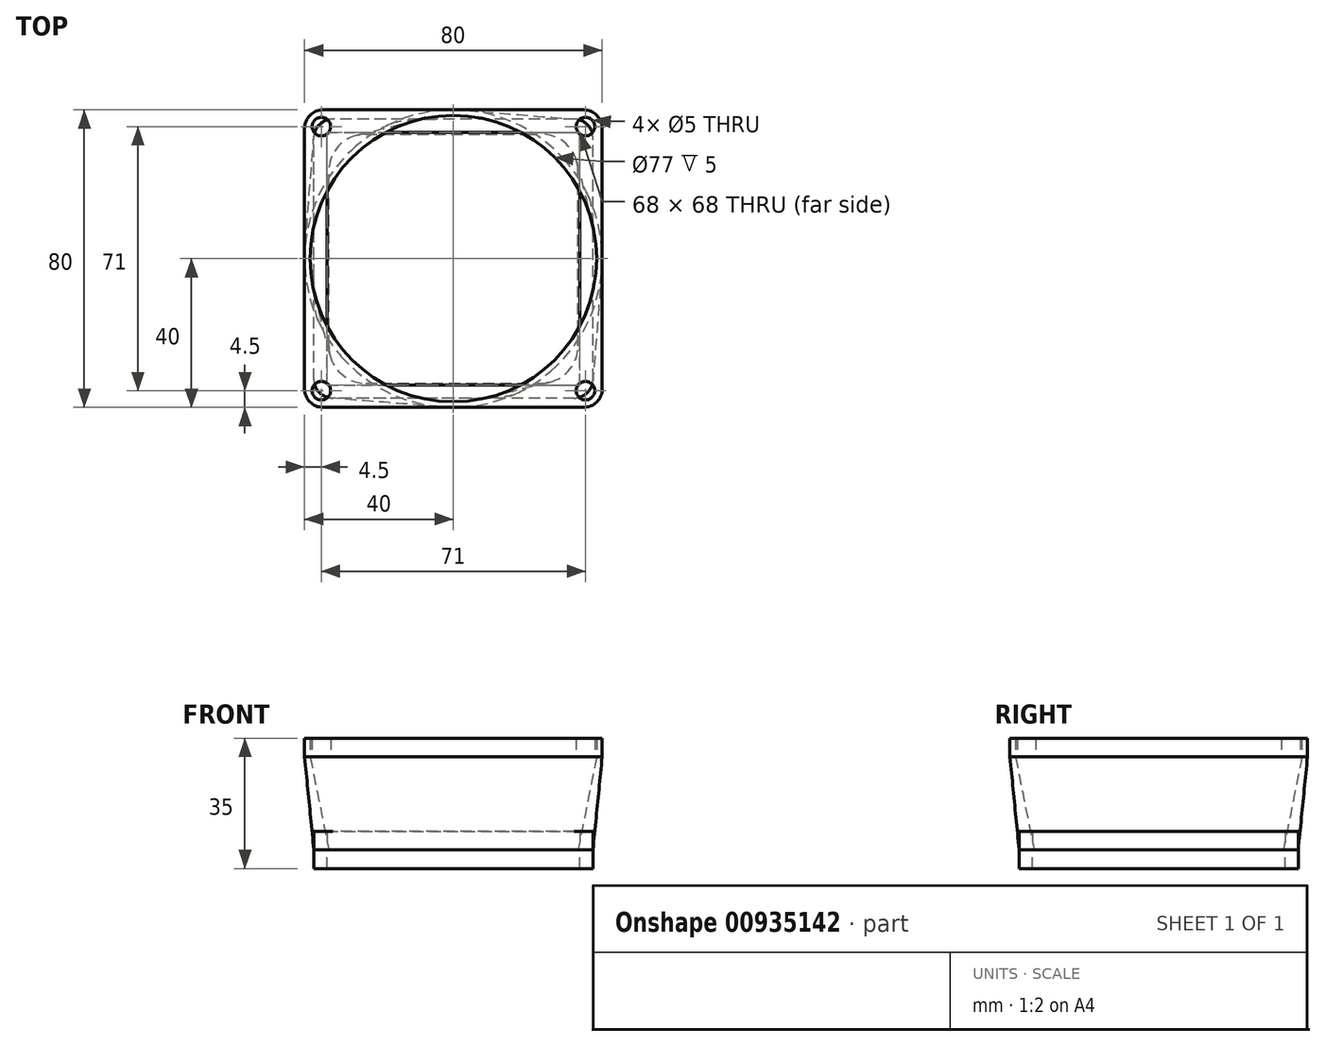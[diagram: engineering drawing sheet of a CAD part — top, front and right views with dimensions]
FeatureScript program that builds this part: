
annotation { "Feature Type Name" : "Feature", "Feature Type Description" : "" }
export const myFeature = defineFeature(function(context is Context, id is Id, definition is map)
    precondition{}
    {
        {
            var Q0;
            Q0=qCreatedBy(makeId("Top.planeOp"),FACE);
            cPlane(context, id + "F0", {"entities" : qUnion([Q0]), "cplaneType" : CPlaneType.OFFSET, "offset" : 25 * mm, "oppositeDirection" : true, "width" : 150 * mm, "height" : 150 * mm});
        }
        {
            var Q0;
            Q0=qCreatedBy(makeId("Top.planeOp"),FACE);
            var sketch = newSketch(context, id + "F1", { "sketchPlane" : qUnion([Q0])});
            skLineSegment(sketch, "E0.bottom", {"start": v(35, -40) * mm, "end": v(-35, -40) * mm});
            skLineSegment(sketch, "E0.top", {"start": v(35, 40) * mm, "end": v(-35, 40) * mm});
            skLineSegment(sketch, "E0.left", {"start": v(40, -35) * mm, "end": v(40, 35) * mm});
            skLineSegment(sketch, "E0.right", {"start": v(-40, -35) * mm, "end": v(-40, 35) * mm});
            skPoint(sketch, "E0.middle", {"position": v(0, 0) * mm});
            skPoint(sketch, "E1.visualSharp", {"position": v(40, -40) * mm});
            skArc(sketch, "E1.filletArc", {"start": v(35, -40) * mm, "mid": v(38.54, -38.54) * mm, "end": v(40, -35) * mm});
            skPoint(sketch, "E2.visualSharp", {"position": v(40, 40) * mm});
            skArc(sketch, "E2.filletArc", {"start": v(40, 35) * mm, "mid": v(38.54, 38.54) * mm, "end": v(35, 40) * mm});
            skPoint(sketch, "E3.visualSharp", {"position": v(-40, 40) * mm});
            skArc(sketch, "E3.filletArc", {"start": v(-35, 40) * mm, "mid": v(-38.54, 38.54) * mm, "end": v(-40, 35) * mm});
            skPoint(sketch, "E4.visualSharp", {"position": v(-40, -40) * mm});
            skArc(sketch, "E4.filletArc", {"start": v(-40, -35) * mm, "mid": v(-38.54, -38.54) * mm, "end": v(-35, -40) * mm});
            skSolve(sketch);
        }
        {
            var Q0;
            Q0=qCreatedBy(id+"F0.planeOp",FACE);
            var sketch = newSketch(context, id + "F2", { "sketchPlane" : qUnion([Q0])});
            skLineSegment(sketch, "E5.bottom", {"start": v(-23.5, -33.5) * mm, "end": v(23.5, -33.5) * mm});
            skLineSegment(sketch, "E5.top", {"start": v(-23.5, 33.5) * mm, "end": v(23.5, 33.5) * mm});
            skLineSegment(sketch, "E5.left", {"start": v(-33.5, -23.5) * mm, "end": v(-33.5, 23.5) * mm});
            skLineSegment(sketch, "E5.right", {"start": v(33.5, -23.5) * mm, "end": v(33.5, 23.5) * mm});
            skPoint(sketch, "E5.middle", {"position": v(0, 0) * mm});
            skPoint(sketch, "E6.visualSharp", {"position": v(-33.5, 33.5) * mm});
            skArc(sketch, "E6.filletArc", {"start": v(-23.5, 33.5) * mm, "mid": v(-30.57, 30.57) * mm, "end": v(-33.5, 23.5) * mm});
            skPoint(sketch, "E7.visualSharp", {"position": v(33.5, 33.5) * mm});
            skArc(sketch, "E7.filletArc", {"start": v(33.5, 23.5) * mm, "mid": v(30.57, 30.57) * mm, "end": v(23.5, 33.5) * mm});
            skPoint(sketch, "E8.visualSharp", {"position": v(33.5, -33.5) * mm});
            skArc(sketch, "E8.filletArc", {"start": v(23.5, -33.5) * mm, "mid": v(30.57, -30.57) * mm, "end": v(33.5, -23.5) * mm});
            skPoint(sketch, "E9.visualSharp", {"position": v(-33.5, -33.5) * mm});
            skArc(sketch, "E9.filletArc", {"start": v(-33.5, -23.5) * mm, "mid": v(-30.57, -30.57) * mm, "end": v(-23.5, -33.5) * mm});
            skSolve(sketch);
        }
        {
            var Q0;
            Q0=qCreatedBy(makeId("Top.planeOp"),FACE);
            var sketch = newSketch(context, id + "F3", { "sketchPlane" : qUnion([Q0])});
            skCircle(sketch, "E10", {"center": v(0, 0) * mm, "radius": 38.5 * mm});
            skSolve(sketch);
        }
        {
            var Q0;
            Q0=qCreatedBy(id+"F0.planeOp",FACE);
            var sketch = newSketch(context, id + "F4", { "sketchPlane" : qUnion([Q0])});
            skLineSegment(sketch, "E11.bottom", {"start": v(32.5, -37.5) * mm, "end": v(-32.5, -37.5) * mm});
            skLineSegment(sketch, "E11.top", {"start": v(32.5, 37.5) * mm, "end": v(-32.5, 37.5) * mm});
            skLineSegment(sketch, "E11.left", {"start": v(37.5, -32.5) * mm, "end": v(37.5, 32.5) * mm});
            skLineSegment(sketch, "E11.right", {"start": v(-37.5, -32.5) * mm, "end": v(-37.5, 32.5) * mm});
            skPoint(sketch, "E11.middle", {"position": v(0, 0) * mm});
            skPoint(sketch, "E12.visualSharp", {"position": v(37.5, -37.5) * mm});
            skArc(sketch, "E12.filletArc", {"start": v(32.5, -37.5) * mm, "mid": v(36.04, -36.04) * mm, "end": v(37.5, -32.5) * mm});
            skPoint(sketch, "E13.visualSharp", {"position": v(37.5, 37.5) * mm});
            skArc(sketch, "E13.filletArc", {"start": v(37.5, 32.5) * mm, "mid": v(36.04, 36.04) * mm, "end": v(32.5, 37.5) * mm});
            skPoint(sketch, "E14.visualSharp", {"position": v(-37.5, 37.5) * mm});
            skArc(sketch, "E14.filletArc", {"start": v(-32.5, 37.5) * mm, "mid": v(-36.04, 36.04) * mm, "end": v(-37.5, 32.5) * mm});
            skPoint(sketch, "E15.visualSharp", {"position": v(-37.5, -37.5) * mm});
            skArc(sketch, "E15.filletArc", {"start": v(-37.5, -32.5) * mm, "mid": v(-36.04, -36.04) * mm, "end": v(-32.5, -37.5) * mm});
            skSolve(sketch);
        }
        {
            var Q0;
            Q0=qCreatedBy(makeId("Top.planeOp"),FACE);
            var sketch = newSketch(context, id + "F5", { "sketchPlane" : qUnion([Q0])});
            skCircle(sketch, "E16", {"center": v(0, 0) * mm, "radius": 40 * mm});
            skSolve(sketch);
        }
        {
            var Q0;
            Q0=qCreatedBy(id+"F0.planeOp",FACE);
            var sketch = newSketch(context, id + "F6", { "sketchPlane" : qUnion([Q0])});
            skLineSegment(sketch, "E17.bottom", {"start": v(-34, -34) * mm, "end": v(34, -34) * mm});
            skLineSegment(sketch, "E17.top", {"start": v(-34, 34) * mm, "end": v(34, 34) * mm});
            skLineSegment(sketch, "E17.left", {"start": v(-34, -34) * mm, "end": v(-34, 34) * mm});
            skLineSegment(sketch, "E17.right", {"start": v(34, -34) * mm, "end": v(34, 34) * mm});
            skPoint(sketch, "E17.middle", {"position": v(0, 0) * mm});
            skSolve(sketch);
        }
        {
            var Q0;
            Q0=qSketchRegion(id+"F8",true);
            var Q1;
            Q1=qSketchRegion(id+"F1",true);
            extrude(context, id + "F7", {"entities" : qUnion([Q0, Q1]), "depth" : 5 * mm, "offsetDistance" : 25 * mm});
        }
        {
            var Q0;
            Q0=qCreatedBy(makeId("Top.planeOp"),FACE);
            var sketch = newSketch(context, id + "F8", { "sketchPlane" : qUnion([Q0])});
            skCircle(sketch, "E18", {"center": v(-35.5, 35.5) * mm, "radius": 2.5 * mm});
            skCircle(sketch, "E19", {"center": v(35.5, 35.5) * mm, "radius": 2.5 * mm});
            skCircle(sketch, "E20", {"center": v(35.5, -35.5) * mm, "radius": 2.5 * mm});
            skCircle(sketch, "E21", {"center": v(-35.5, -35.5) * mm, "radius": 2.5 * mm});
            skSolve(sketch);
        }
        {
            var Q0;
            Q0=qSketchRegion(id+"F3",true);
            var Q1;
            Q1=qSketchRegion(id+"F6",true);
            var Q2;
            Q2=qSketchRegion(id+"F4",true);
            extrude(context, id + "F9", {"entities" : qUnion([Q0, Q1, Q2]), "depth" : 5 * mm, "offsetDistance" : 25 * mm});
        }
        {
            var Q0;
            Q0=qSketchRegion(id+"F8",true);
            extrude(context, id + "F10", {"entities" : qUnion([Q0]), "depth" : 5 * mm, "offsetDistance" : 25 * mm});
        }
        {
            var Q0;
            Q0=makeQuery(id+"F9.opExtrude","SWEPT_BODY",BODY,{"disambiguationData":[OSD([sQuery(id+"F3.wireOp",EDGE,"E10")])]});
            var Q1;
            Q1=makeQuery(id+"F10.opExtrude","SWEPT_BODY",BODY,{"disambiguationData":[OSD([sQuery(id+"F8.wireOp",EDGE,"E19")])]});
            var Q2;
            Q2=makeQuery(id+"F10.opExtrude","SWEPT_BODY",BODY,{"disambiguationData":[OSD([sQuery(id+"F8.wireOp",EDGE,"E21")])]});
            var Q3;
            Q3=makeQuery(id+"F10.opExtrude","SWEPT_BODY",BODY,{"disambiguationData":[OSD([sQuery(id+"F8.wireOp",EDGE,"E18")])]});
            var Q4;
            Q4=makeQuery(id+"F10.opExtrude","SWEPT_BODY",BODY,{"disambiguationData":[OSD([sQuery(id+"F8.wireOp",EDGE,"E20")])]});
            var Q5;
            Q5=makeQuery(id+"F7.opExtrude","SWEPT_BODY",BODY,{"disambiguationData":[OSD([sQuery(id+"F1.wireOp",EDGE,"E0.bottom"),sQuery(id+"F1.wireOp",EDGE,"E0.top"),sQuery(id+"F1.wireOp",EDGE,"E0.left"),sQuery(id+"F1.wireOp",EDGE,"E0.right"),sQuery(id+"F1.wireOp",EDGE,"E1.filletArc"),sQuery(id+"F1.wireOp",EDGE,"E2.filletArc"),sQuery(id+"F1.wireOp",EDGE,"E3.filletArc"),sQuery(id+"F1.wireOp",EDGE,"E4.filletArc")])]});
            booleanBodies(context, id + "F11", {"operationType" : BooleanOperationType.SUBTRACTION, "tools" : qUnion([Q0, Q1, Q2, Q3, Q4]), "targets" : qUnion([Q5])});
        }
        {
            var Q0;
            Q0=qSketchRegion(id+"F3",true);
            var Q1;
            Q1=qSketchRegion(id+"F2",true);
            loft(context, id + "F12", {"sheetProfilesArray" : [{ "sheetProfileEntities" : qUnion([Q0]) }, { "sheetProfileEntities" : qUnion([Q1]) }]});
        }
        {
            var Q0;
            Q0=qSketchRegion(id+"F5",true);
            var Q1;
            Q1=qSketchRegion(id+"F4",true);
            loft(context, id + "F13", {"sheetProfilesArray" : [{ "sheetProfileEntities" : qUnion([Q0]) }, { "sheetProfileEntities" : qUnion([Q1]) }]});
        }
        {
            var Q0;
            Q0=makeQuery(id+"F12.opLoft","SWEPT_BODY",BODY,{"disambiguationData":[OSD([makeQuery(id+"F2.imprint","IMPRINT",FACE,{"disambiguationData":[TD([[makeQuery(id+"F2.imprint","IMPRINT",EDGE,{"derivedFrom":sQuery(id+"F2.wireOp",EDGE,"E5.bottom")}),1.0]])]}),makeQuery(id+"F3.imprint","IMPRINT",FACE,{"disambiguationData":[TD([[makeQuery(id+"F3.imprint","IMPRINT",EDGE,{"derivedFrom":sQuery(id+"F3.wireOp",EDGE,"E10")}),1.0]])]})])]});
            var Q1;
            Q1=makeQuery(id+"F13.opLoft","SWEPT_BODY",BODY,{"disambiguationData":[OSD([makeQuery(id+"F4.imprint","IMPRINT",FACE,{"disambiguationData":[TD([[makeQuery(id+"F4.imprint","IMPRINT",EDGE,{"derivedFrom":sQuery(id+"F4.wireOp",EDGE,"E11.bottom")}),-1.0]])]}),makeQuery(id+"F5.imprint","IMPRINT",FACE,{"disambiguationData":[TD([[makeQuery(id+"F5.imprint","IMPRINT",EDGE,{"derivedFrom":sQuery(id+"F5.wireOp",EDGE,"E16")}),1.0]])]})])]});
            booleanBodies(context, id + "F14", {"operationType" : BooleanOperationType.SUBTRACTION, "tools" : qUnion([Q0]), "targets" : qUnion([Q1])});
        }
        {
            var Q0;
            Q0=makeQuery(id+"F4.imprint","IMPRINT",FACE,{"disambiguationData":[TD([[makeQuery(id+"F4.imprint","IMPRINT",EDGE,{"derivedFrom":sQuery(id+"F4.wireOp",EDGE,"E11.bottom")}),-1.0]])]});
            extrude(context, id + "F15", {"entities" : qUnion([Q0]), "oppositeDirection" : true, "depth" : 5 * mm, "offsetDistance" : 25 * mm});
        }
        {
            var Q0;
            Q0=qSketchRegion(id+"F6",true);
            extrude(context, id + "F16", {"entities" : qUnion([Q0]), "oppositeDirection" : true, "depth" : 10 * mm, "offsetDistance" : 25 * mm});
        }
        {
            var Q0;
            Q0=makeQuery(id+"F16.opExtrude","SWEPT_BODY",BODY,{"disambiguationData":[OSD([sQuery(id+"F6.wireOp",EDGE,"E17.bottom"),sQuery(id+"F6.wireOp",EDGE,"E17.top"),sQuery(id+"F6.wireOp",EDGE,"E17.left"),sQuery(id+"F6.wireOp",EDGE,"E17.right")])]});
            var Q1;
            Q1=makeQuery(id+"F15.opExtrude","SWEPT_BODY",BODY,{"disambiguationData":[OSD([sQuery(id+"F4.wireOp",EDGE,"E11.bottom"),sQuery(id+"F4.wireOp",EDGE,"E11.top"),sQuery(id+"F4.wireOp",EDGE,"E11.left"),sQuery(id+"F4.wireOp",EDGE,"E11.right"),sQuery(id+"F4.wireOp",EDGE,"E12.filletArc"),sQuery(id+"F4.wireOp",EDGE,"E13.filletArc"),sQuery(id+"F4.wireOp",EDGE,"E14.filletArc"),sQuery(id+"F4.wireOp",EDGE,"E15.filletArc")])]});
            booleanBodies(context, id + "F17", {"operationType" : BooleanOperationType.SUBTRACTION, "tools" : qUnion([Q0]), "targets" : qUnion([Q1])});
        }
    });
